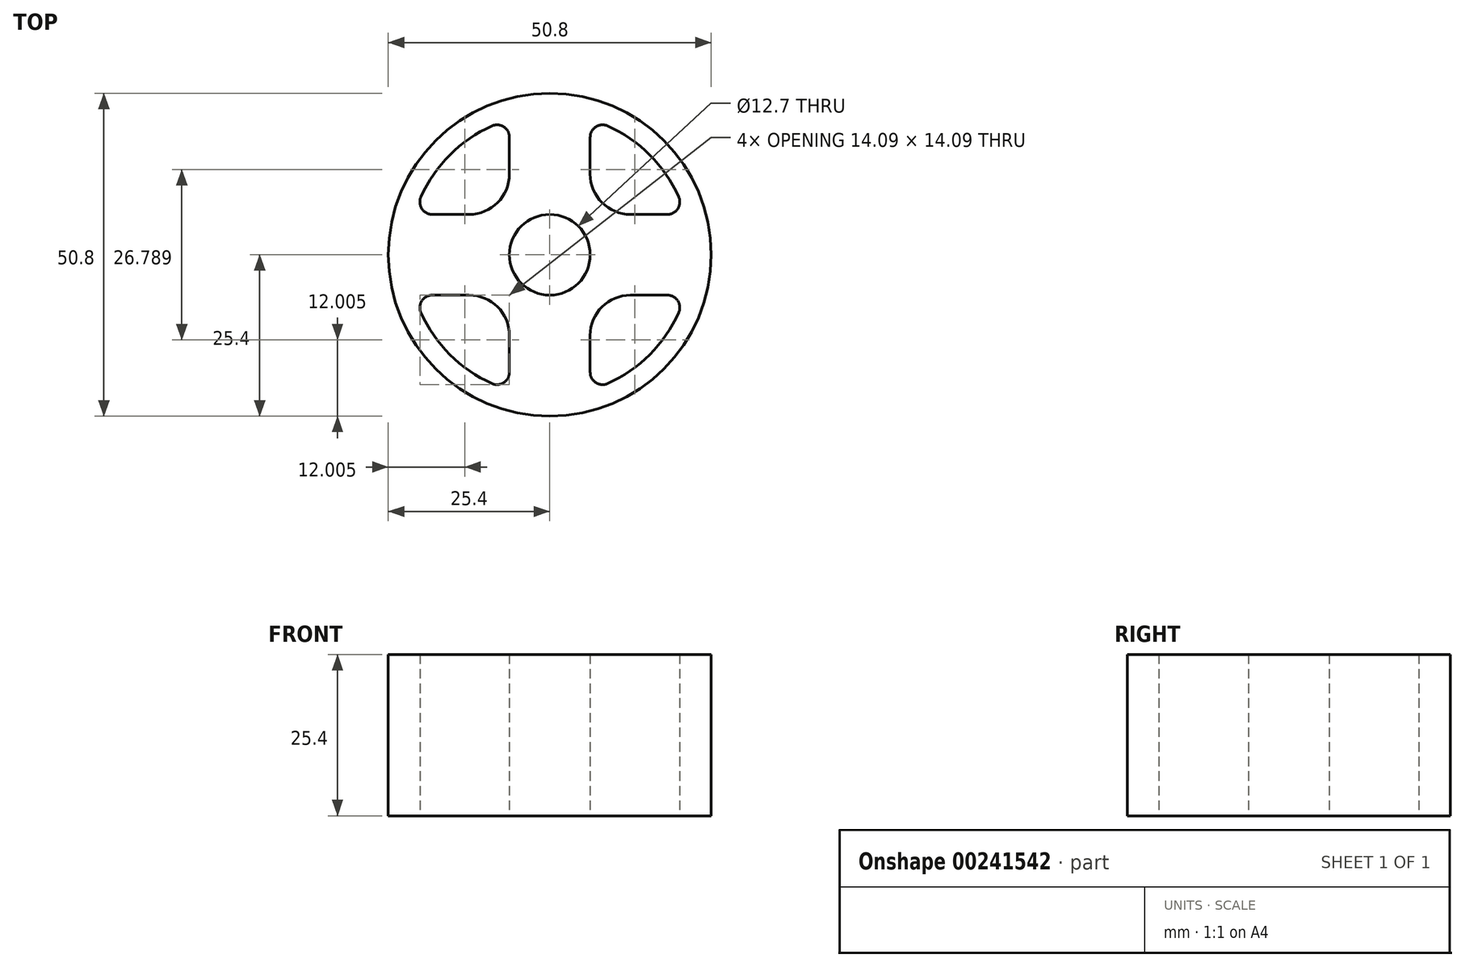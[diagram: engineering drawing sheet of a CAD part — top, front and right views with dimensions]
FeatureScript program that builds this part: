
annotation { "Feature Type Name" : "Feature", "Feature Type Description" : "" }
export const myFeature = defineFeature(function(context is Context, id is Id, definition is map)
    precondition{}
    {
        {
            var Q0;
            Q0=qCreatedBy(makeId("Top.planeOp"),FACE);
            var sketch = newSketch(context, id + "F0", { "sketchPlane" : qUnion([Q0])});
            skCircle(sketch, "E0", {"center": v(0, 0) * mm, "radius": 6.35 * mm});
            skArc(sketch, "E1", {"start": v(-20.27, -9.1) * mm, "mid": v(-15.72, -15.72) * mm, "end": v(-9.1, -20.27) * mm});
            skCircle(sketch, "E2", {"center": v(0, 0) * mm, "radius": 25.4 * mm});
            skLineSegment(sketch, "E3", {"start": v(0, 0) * mm, "end": v(0, 22.23) * mm});
            skLineSegment(sketch, "E4.0", {"start": v(6.35, 12.7) * mm, "end": v(6.35, 18.49) * mm});
            skLineSegment(sketch, "E5.0", {"start": v(-6.35, 12.7) * mm, "end": v(-6.35, 18.49) * mm});
            skLineSegment(sketch, "E6", {"start": v(0, 0) * mm, "end": v(-22.23, 0) * mm});
            skLineSegment(sketch, "E7.0", {"start": v(-12.7, 6.35) * mm, "end": v(-18.49, 6.35) * mm});
            skLineSegment(sketch, "E8.0", {"start": v(-12.7, -6.35) * mm, "end": v(-18.49, -6.35) * mm});
            skLineSegment(sketch, "E9", {"start": v(0, 0) * mm, "end": v(0, -22.23) * mm});
            skLineSegment(sketch, "E10.0", {"start": v(-6.35, -12.7) * mm, "end": v(-6.35, -18.49) * mm});
            skLineSegment(sketch, "E11.0", {"start": v(6.35, -12.7) * mm, "end": v(6.35, -18.49) * mm});
            skLineSegment(sketch, "E12", {"start": v(0, 0) * mm, "end": v(22.23, 0) * mm});
            skLineSegment(sketch, "E13.0", {"start": v(12.7, -6.35) * mm, "end": v(18.49, -6.35) * mm});
            skLineSegment(sketch, "E14.0", {"start": v(12.7, 6.35) * mm, "end": v(18.49, 6.35) * mm});
            skArc(sketch, "E15.trimOffspring", {"start": v(-9.1, 20.27) * mm, "mid": v(-15.72, 15.72) * mm, "end": v(-20.27, 9.1) * mm});
            skArc(sketch, "E16.trimOffspring", {"start": v(20.27, 9.1) * mm, "mid": v(15.72, 15.72) * mm, "end": v(9.1, 20.27) * mm});
            skArc(sketch, "E17.trimOffspring", {"start": v(9.1, -20.27) * mm, "mid": v(15.72, -15.72) * mm, "end": v(20.27, -9.1) * mm});
            skPoint(sketch, "E18.visualSharp", {"position": v(6.35, 6.35) * mm});
            skArc(sketch, "E18.filletArc", {"start": v(6.35, 12.7) * mm, "mid": v(8.2, 8.2) * mm, "end": v(12.7, 6.35) * mm});
            skPoint(sketch, "E19.visualSharp", {"position": v(6.35, -6.35) * mm});
            skArc(sketch, "E19.filletArc", {"start": v(12.7, -6.35) * mm, "mid": v(8.2, -8.2) * mm, "end": v(6.35, -12.7) * mm});
            skPoint(sketch, "E20.visualSharp", {"position": v(-6.35, -6.35) * mm});
            skArc(sketch, "E20.filletArc", {"start": v(-6.35, -12.7) * mm, "mid": v(-8.2, -8.2) * mm, "end": v(-12.7, -6.35) * mm});
            skPoint(sketch, "E21.visualSharp", {"position": v(-6.35, 6.35) * mm});
            skArc(sketch, "E21.filletArc", {"start": v(-12.7, 6.35) * mm, "mid": v(-8.2, 8.2) * mm, "end": v(-6.35, 12.7) * mm});
            skPoint(sketch, "E22.visualSharp", {"position": v(6.35, 21.3) * mm});
            skArc(sketch, "E22.filletArc", {"start": v(9.1, 20.27) * mm, "mid": v(7.24, 20.13) * mm, "end": v(6.35, 18.49) * mm});
            skPoint(sketch, "E23.visualSharp", {"position": v(21.3, 6.35) * mm});
            skArc(sketch, "E23.filletArc", {"start": v(18.49, 6.35) * mm, "mid": v(20.13, 7.24) * mm, "end": v(20.27, 9.1) * mm});
            skPoint(sketch, "E24.visualSharp", {"position": v(21.3, -6.35) * mm});
            skArc(sketch, "E24.filletArc", {"start": v(20.27, -9.1) * mm, "mid": v(20.13, -7.24) * mm, "end": v(18.49, -6.35) * mm});
            skPoint(sketch, "E25.visualSharp", {"position": v(6.35, -21.3) * mm});
            skArc(sketch, "E25.filletArc", {"start": v(6.35, -18.49) * mm, "mid": v(7.24, -20.13) * mm, "end": v(9.1, -20.27) * mm});
            skPoint(sketch, "E26.visualSharp", {"position": v(-6.35, -21.3) * mm});
            skArc(sketch, "E26.filletArc", {"start": v(-9.1, -20.27) * mm, "mid": v(-7.24, -20.13) * mm, "end": v(-6.35, -18.49) * mm});
            skPoint(sketch, "E27.visualSharp", {"position": v(-21.3, -6.35) * mm});
            skArc(sketch, "E27.filletArc", {"start": v(-18.49, -6.35) * mm, "mid": v(-20.13, -7.24) * mm, "end": v(-20.27, -9.1) * mm});
            skPoint(sketch, "E28.visualSharp", {"position": v(-21.3, 6.35) * mm});
            skArc(sketch, "E28.filletArc", {"start": v(-20.27, 9.1) * mm, "mid": v(-20.13, 7.24) * mm, "end": v(-18.49, 6.35) * mm});
            skPoint(sketch, "E29.visualSharp", {"position": v(-6.35, 21.3) * mm});
            skArc(sketch, "E29.filletArc", {"start": v(-6.35, 18.49) * mm, "mid": v(-7.24, 20.13) * mm, "end": v(-9.1, 20.27) * mm});
            skSolve(sketch);
        }
        {
            var Q0;
            Q0 = qSketchRegion(id + "F0", true);
            extrude(context, id + "F1", {"entities" : qUnion([Q0]), "endBound" : BoundingType.SYMMETRIC, "depth" : 25.4 * mm});
        }
    });
